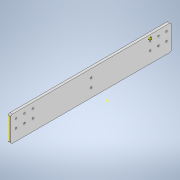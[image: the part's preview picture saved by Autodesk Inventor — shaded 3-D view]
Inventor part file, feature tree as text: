
AUTODESK INVENTOR PART (.ipt)
format: ipt  version: 2021 (Build 250183000, 183)  size: 260,608 bytes
history: native  units: mm
features: sketch x28, extrude x24, fillet x1
ambient origin geometry x8: Origin, YZ Plane, XZ Plane, XY Plane, X Axis, Y Axis, Z Axis, Center Point
bodies: Solid1 (feature_tree)
feature tree (53):
  extrude  "Extrusion1"  Depth=190.0mm
  extrude  "Extrusion3"  Depth=3.0mm
  extrude  "Extrusion4"  Depth=1.0mm TaperAngle=0.0deg
  extrude  "Extrusion5"  Depth=2.0mm TaperAngle=0.0deg
  extrude  "Extrusion6"  Depth=2.0mm
  extrude  "Extrusion11"  Depth=1.0mm TaperAngle=0.0deg
  fillet  "Fillet1"  Radius=2.0mm
  extrude  "Extrusion16"  Depth=1.0mm TaperAngle=0.0deg
  extrude  "Extrusion17"  Depth=2.0mm
  extrude  "Extrusion19"  Depth=2.0mm
  extrude  "Extrusion20"  Depth=9.520792mm
  extrude  "Extrusion21"  Depth=1.0mm TaperAngle=0.0deg
  extrude  "Extrusion22"  Depth=2.0mm TaperAngle=0.0deg
  sketch  "Sketch25"  dims[d85=3.0mm d86=0.0mm d87=4.0mm]
  sketch  "Sketch26"  dims[d88=1.0mm d89=0.0mm d90=10.0mm]
  sketch  "Sketch27"  dims[d91=1.0mm d92=0.0mm d93=10.0mm]
  extrude  "Extrusion23"  Depth=9.806614mm
  extrude  "Extrusion24"  Depth=2.0mm
  sketch  "Sketch28"  dims[d95=1.0mm d96=0.0mm d97=10.0mm]
  extrude  "Extrusion25"  Depth=1.0mm TaperAngle=0.0deg
  sketch  "Sketch30"  dims[d100=1.0mm d101=0.0mm d102=1.0mm d103=0.0mm]
  extrude  "Extrusion26"  Depth=2.0mm TaperAngle=0.0deg
  extrude  "Extrusion27"  Depth=2.0mm
  sketch  "Sketch33"  dims[d108=4.0mm d109=4.0mm d110=6.0mm d111=1.0mm d112=0.0mm d113=2.0mm d114=0.0mm]
  sketch  "Sketch2"  dims[d0=30.0mm d1=190.0mm]
  sketch  "Sketch4"  dims[d2=3.0mm d3=0.0mm d7=4.0mm]
  sketch  "Sketch5"  dims[d8=6.0mm d9=1.0mm d10=0.0mm]
  sketch  "Sketch6"  dims[d11=2.0mm d12=2.0mm d13=0.0mm]
  sketch  "Sketch7"  dims[d14=2.0mm d15=4.0mm]
  sketch  "Sketch12"  dims[d32=4.0mm d33=2.0mm d34=10.0mm d36=0.0mm d37=1.0mm d42=2.0mm]
  sketch  "Sketch18"  dims[d58=4.0mm d59=2.0mm d60=10.0mm d62=0.0mm d63=1.0mm d64=2.0mm d66=0.0mm d67=2.0mm]
  sketch  "Sketch19"  dims[d68=9.860446mm d69=9.806614mm]
  sketch  "Sketch21"  dims[d71=9.806614mm d72=2.0mm]
  sketch  "Sketch22"  dims[d73=4.0mm d74=1.0mm d75=0.0mm]
  sketch  "Sketch23"  dims[d76=2.0mm d77=2.0mm d78=0.0mm]
  sketch  "Sketch24"  dims[d79=6.0mm d84=2.0mm]
  sketch  "Sketch29"  dims[d98=10.0mm d99=10.0mm]
  sketch  "Sketch31"  dims[d104=2.0mm d105=2.0mm]
  sketch  "Sketch32"  dims[d106=2.0mm d107=0.0mm]
  sketch  "Sketch8"  dims[d17=10.0mm d18=1.0mm d19=0.0mm d20=2.0mm]
  sketch  "Sketch9"  dims[d21=2.0mm d22=0.0mm d23=4.0mm d24=6.0mm d26=0.0mm d27=1.0mm]
  sketch  "Sketch10"  dims[d28=2.0mm d30=0.0mm d31=2.0mm]
  sketch  "Sketch14"  dims[d43=2.0mm d44=0.0mm d45=9.471719mm]
  sketch  "Sketch15"  dims[d46=9.471719mm d47=9.520792mm]
  sketch  "Sketch16"  dims[d48=9.520792mm d49=4.0mm d50=6.0mm d52=0.0mm d53=1.0mm]
  sketch  "Sketch17"  dims[d54=2.0mm d56=0.0mm d57=2.0mm]
  extrude  "Extrusion7"  Depth=3.0mm
  extrude  "Extrusion8"  Depth=10.0mm
  extrude  "Extrusion9"  Depth=10.0mm
  extrude  "Extrusion12"  Depth=10.0mm
  extrude  "Extrusion13"  Depth=10.0mm
  extrude  "Extrusion14"  Depth=1.0mm TaperAngle=0.0deg
  extrude  "Extrusion15"  Depth=2.0mm
